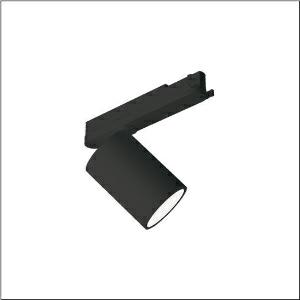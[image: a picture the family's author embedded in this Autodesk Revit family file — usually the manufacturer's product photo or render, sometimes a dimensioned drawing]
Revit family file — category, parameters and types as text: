
# Revit family: spot_31_51sf32mab4b
name_source: partatom
category: Lighting Fixtures
units: mm (PartAtom-declared; Revit-internal decimal feet)

## family parameters
Cut with Voids When Loaded = No
Host = Face
Light Source = No
Part Type = Normal
Room Calculation Point = No
Round Connector Dimension = Use Diameter
Shared = No

## types (1)
- --- (1 x LED, 4980 lm, 41.8 W, 3000K)
    Apparent Load = 42 VA
    CIE Flux Codes = 93 97 99 100 100
    Color Rendering = 90
    Color Temperature = 3000K
    Default Elevation = 1800 mm
    Description = Spot 31, directional spotlight, light control with lens, of PMMA, LED rated luminous flux: 4.790lm, light colour: 930, control gear: ECG Multilumen, with 3-phase adapter, mains connection: 220..240V, AC, 50/60Hz, of aluminium, jet black (RAL 9005), length: 213mm, diameter: 90mm, protection rating (complete): IP20, insulation class (complete): insulation class I (protective earthing), certification: CE, impact resistance: IK02, permissible ambient temperature for indoor applications: -20..+40°C, packaging unit: 1 piece
    Height = 175 mm
    Lamp = 1 x LED
    Lamp Light Flux = 4980 lm
    Lamp Power = 41.8 W
    Lamp count = 1
    Length = 90 mm
    Luminous efficacy = 119 lm/W
    Manufacturer = Siteco
    ModVariant = No
    Model = 51SF32MAB4B
    Mounting Place = Ceiling
    Mounting Type = Pendant
    Number of Poles = 1
    OnlyDefault = Yes
    Power Factor = 1
    Product Name = Spot 31
    Product group = directional spotlight
    ProductGroupID = 905
    Protection Class = Protection class I
    Protection Degree = IP 20
    RLX_Detail_Level = 1
    RLX_Emergency_Light_Flux = 0 lm
    RLX_Emergency_Type = 0
    RLX_Emergency_Type_DB = No
    RlxData = <blob elided: 20909 chars, md5=9d83dfb0>
    Socket = socket
    Standby Power = 0 W
    System Light Flux = 4980 lm
    System Power = 42 W
    Type Comments = factory setting: luminous flux: 100 % | (ON | ON | ON | ON) | 1050 mA
    Type Image = l_1273723.jpg
    URL = http://relux.com
    VarID = @adj_096243
    Voltage = 0 V
    Weight = 0.00 kg
    Width = 0 mm  [stored 0 ft]

note: [stored X ft] marks values corroborated as IEEE doubles in the binary element streams (Revit-internal decimal feet)

## geometry (parser evidence)
native form markers: Blend x4, Sweep x11
no freeform markers — native parametric forms only
